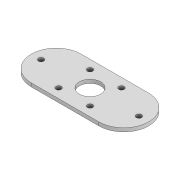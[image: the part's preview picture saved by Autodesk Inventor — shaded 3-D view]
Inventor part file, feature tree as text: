
AUTODESK INVENTOR PART (.ipt)
format: ipt  version: 2022 (Build 260153000, 153)  size: 137,216 bytes
history: native  units: mm
features: extrude x1, sketch x1, projected_geometry x1
ambient origin geometry x8: Origin, YZ Plane, XZ Plane, XY Plane, X Axis, Y Axis, Z Axis, Center Point
bodies: Body1 (feature_tree)
feature tree (3):
  extrude  "Extrusion2"  Depth=28.0mm
  sketch  "Sketch3"  dims[d37=3.0mm d38=3.0mm d39=3.0mm d40=3.0mm d41=12.5mm d42=12.5mm d43=12.5mm d44=12.5mm d55=2.0mm d56=0.0mm d60=28.0mm d61=12.0mm d66=5.0mm d67=5.0mm d68=3.0mm d69=3.0mm d70=8.5mm d71=8.5mm]
  projected_geometry  "Projected Loop1"
